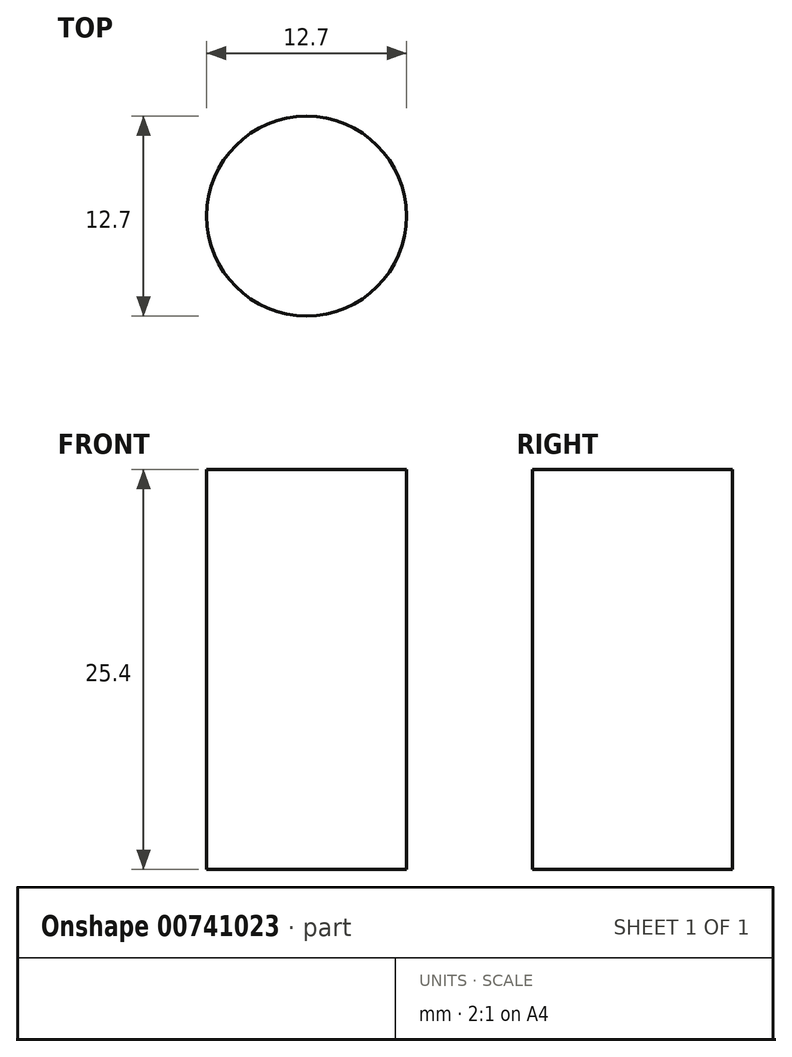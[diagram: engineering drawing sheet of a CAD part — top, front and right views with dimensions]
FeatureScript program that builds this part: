
annotation { "Feature Type Name" : "Feature", "Feature Type Description" : "" }
export const myFeature = defineFeature(function(context is Context, id is Id, definition is map)
    precondition{}
    {
        {
            var Q0;
            Q0=qCreatedBy(makeId("Top.planeOp"),FACE);
            var sketch = newSketch(context, id + "F0", { "sketchPlane" : qUnion([Q0])});
            skCircle(sketch, "E0", {"center": v(0, 0) * mm, "radius": 6.35 * mm});
            skSolve(sketch);
        }
        {
            var Q0;
            Q0=makeQuery(id+"F0.imprint","IMPRINT",FACE,{"disambiguationData":[TD([[makeQuery(id+"F0.imprint","IMPRINT",EDGE,{"derivedFrom":sQuery(id+"F0.wireOp",EDGE,"E0")}),1.0]])]});
            extrude(context, id + "F1", {"entities" : qUnion([Q0]), "depth" : 25.4 * mm, "offsetDistance" : 25.4 * mm});
        }
    });
